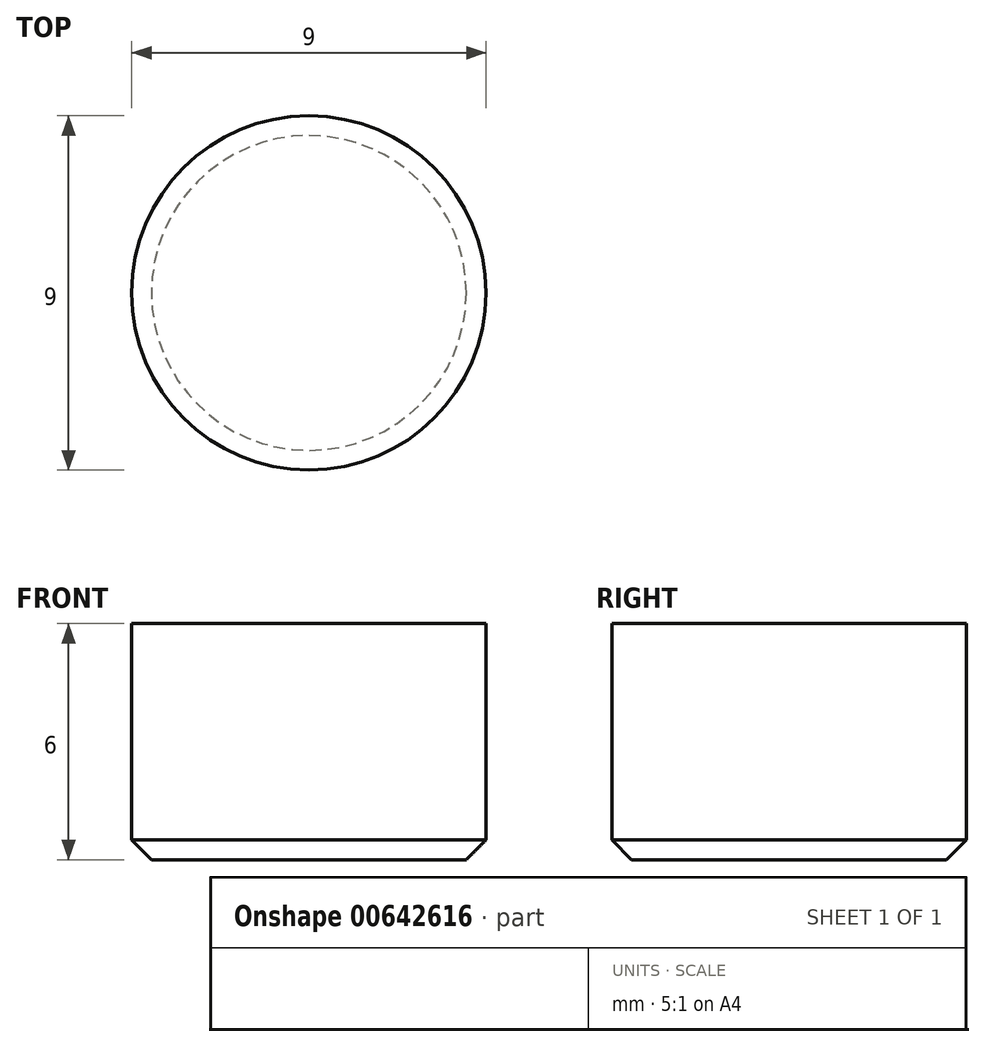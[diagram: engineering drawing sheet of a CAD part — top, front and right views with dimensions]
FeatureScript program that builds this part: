
annotation { "Feature Type Name" : "Feature", "Feature Type Description" : "" }
export const myFeature = defineFeature(function(context is Context, id is Id, definition is map)
    precondition{}
    {
        {
            var Q0;
            Q0=qCreatedBy(makeId("Top.planeOp"),FACE);
            var sketch = newSketch(context, id + "F0", { "sketchPlane" : qUnion([Q0])});
            skCircle(sketch, "E0", {"center": v(0, 0) * mm, "radius": 7.2 * mm});
            skSolve(sketch);
        }
        {
            var Q0;
            Q0=makeQuery(id+"F0.imprint","IMPRINT",FACE,{"disambiguationData":[TD([[makeQuery(id+"F0.imprint","IMPRINT",EDGE,{"derivedFrom":sQuery(id+"F0.wireOp",EDGE,"E0")}),1.0]])]});
            extrude(context, id + "F1", {"entities" : qUnion([Q0]), "depth" : 6 * mm, "offsetDistance" : 25 * mm});
        }
        {
            var Q0;
            Q0=makeQuery(id+"F1.opExtrude","CAP_FACE",FACE,{"disambiguationData":[OSD([sQuery(id+"F0.wireOp",EDGE,"E0")])],"isStart":false});
            var sketch = newSketch(context, id + "F2", { "sketchPlane" : qUnion([Q0])});
            skCircle(sketch, "E1", {"center": v(0, 0) * mm, "radius": 4.5 * mm});
            skSolve(sketch);
        }
        {
            var Q0;
            Q0=makeQuery(id+"F2.imprint","IMPRINT",FACE,{"disambiguationData":[TD([[makeQuery(id+"F2.imprint","IMPRINT",EDGE,{"derivedFrom":sQuery(id+"F2.wireOp",EDGE,"E1")}),-1.0]])]});
            extrude(context, id + "F3", {"entities" : qUnion([Q0]), "operationType" : NewBodyOperationType.REMOVE, "oppositeDirection" : true, "depth" : 25 * mm, "offsetDistance" : 25 * mm});
        }
        {
            var Q0;
            Q0=makeQuery(id+"F3.boolean.opBoolean","COPY",EDGE,{"derivedFrom":makeQuery(id+"F3.opExtrude","CAP_EDGE",EDGE,{"disambiguationData":[OSD([sQuery(id+"F2.wireOp",EDGE,"E1")])],"isStart":true})});
            var Q1;
            Q1=makeQuery(id+"F3.boolean.opBoolean","INTERSECT",EDGE,{"derivedFrom":[makeQuery(id+"F1.opExtrude","CAP_FACE",FACE,{"disambiguationData":[OSD([sQuery(id+"F0.wireOp",EDGE,"E0")])],"isStart":true}),makeQuery(id+"F3.opExtrude","SWEPT_FACE",FACE,{"disambiguationData":[OSD([sQuery(id+"F2.wireOp",EDGE,"E1")])]})]});
            chamfer(context, id + "F4", {"entities" : qUnion([Q0, Q1]), "chamferType" : ChamferType.OFFSET_ANGLE, "width" : 0.5 * mm, "oppositeDirection" : false, "angle" : 45 * degree, "tangentPropagation" : true});
        }
    });
